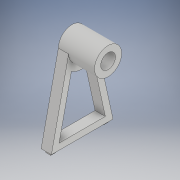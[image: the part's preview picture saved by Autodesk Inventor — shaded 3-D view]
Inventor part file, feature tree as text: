
AUTODESK INVENTOR PART (.ipt)
format: ipt  version: 2019 (Build 230136000, 136)  size: 183,296 bytes
history: native  units: in
note: dims shown in document units (in); Inventor stores cm internally (conversion verified against a paired STEP export)
features: sketch x7, extrude x6, projected_geometry x4
ambient origin geometry x8: Origin, YZ Plane, XZ Plane, XY Plane, X Axis, Y Axis, Z Axis, Center Point
bodies: Solid1 (feature_tree)
feature tree (17):
  extrude  "Extrusion1"  Depth=0.15in
  extrude  "Extrusion2"  Depth=0.1in TaperAngle=0.0deg
  extrude  "Extrusion3"  Depth=0.75in
  sketch  "Sketch6"  dims[d8=0.15in d9=0.25in d10=0.0in]
  extrude  "Extrusion7"  Depth=0.25in TaperAngle=0.0deg
  extrude  "Extrusion9"  Depth=0.875in TaperAngle=0.0deg
  extrude  "Extrusion10"  Depth=0.115in
  sketch  "Sketch1"  dims[d0=0.36in d1=0.15in]
  sketch  "Sketch2"  dims[d2=0.78in d3=0.0in d4=0.1in d5=0.0in]
  sketch  "Sketch3"  dims[d6=1.5in d7=0.75in]
  sketch  "Sketch10"  dims[d20=0.5315in d28=0.875in d29=0.0in]
  sketch  "Sketch13"  dims[d32=0.115in d33=0.115in]
  sketch  "Sketch14"  dims[d34=0.0675in d35=0.05in d36=0.115in d37=0.115in d38=0.068in d39=0.05in d40=0.075in d41=0.0in d42=0.0in d43=0.0in d44=0.0in d45=0.1in d46=0.0in]
  projected_geometry  "Projected Loop9"
  projected_geometry  "Projected Loop10"
  projected_geometry  "Projected Loop11"
  projected_geometry  "Projected Loop12"
